# Revit family: Тактильная плитка полиуретан (самоклеящаяся)
name_source: partatom
category: Оборудование
revit_build: Autodesk Revit 2017 (Build: 20160225_1515(x64)
units: mm (PartAtom-declared; Revit-internal decimal feet)

## family parameters
Общий = Да
Основа = Грань
При загрузке вырезать с полостями = Да
Размер круглого соединителя = Использовать диаметр
Тип детали = Нормальный
Точка расчета площади = Нет

## types (2) — shared parameters
ADSK_Наименование = Тактильная плитка полиуретан (самоклеящаяся)
ADSK_Размер_Высота рифа = 5 мм
ADSK_Размер_Габариты = 300Х300
ADSK_Размер_Длина = 300 мм
ADSK_Размер_Толщина = 2 мм
ADSK_Размер_Ширина = 300 мм
ADSK_Тип рифов = Тактильные конусообразные рифы в шахматном порядке
URL = http://tiflocentre.ru
Изготовитель = ТИФЛОЦЕНТР «ВЕРТИКАЛЬ»
Применение = Улица/Помещение
Стоимость = 742 $
zero-valued in all types: Отметка по умолчанию

## per-type parameters (varying)
| type | ADSK_Код изделия | ADSK_Материал наименование | ADSK_Материал плитки | Описание |
| Тактильная плитка полиуретан (самоклеящаяся)_Желтая | 10129-1-ZH | Полиуретан, цвет желтый | Вертикаль_Полиуретан_Желтый | Тактильная плитка ПУ предназначена для информирования людей с ограничениями зрения о движении. Желтый цвет плитки - отличный контраст к поверхности, который необходимо организовать для людей с ограниченными возможностями. Тактильные конусообразные рифы в шахматном порядке информируют незрячего человека о непреодолимых препятствиях на пути. Тактильная ПУ плитка имеет ряд преимуществ: стойкость к перепадам температур, износостойкость и легкость монтажа (самоклеящаяся). Тактильная ПУ плитка от Тифлоцентра "Вертикаль" рекомендован к применению Всероссийским обществом слепых, а также государственной федеральной программой "Доступная среда". |
| Тактильная плитка полиуретан (самоклеющаяся)_Черная | 10129-1-CH | Полиуретан, цвет черный | Вертикаль_Полиуретан_Черный | Тактильная ПУ плитка применятеся для информирования при движении тотально слепого и слабовидящего человека. Конусообразные рифы в шахматном порядке на плитке "предупреждают" человека о непреодолимом препятствии на пути. В случаях, когда монтаж плитки приходится на светлую поверхность, черная плитка обладает большим контрастом, чем желтая. Это особенно важно для слабовидящих людей. Главные преимущества тактильной ПУ плитки: всепогодность, прочность и легкость монтажа. Монтировать тактильную плитку от компании "Вертикаль" мы рекомендуем на специальный клей FIXVERT, состав которого разработан и протестирован нашими специалистами. |
